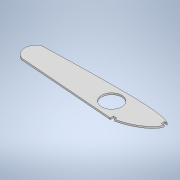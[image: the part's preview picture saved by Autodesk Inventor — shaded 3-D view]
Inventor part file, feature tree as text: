
AUTODESK INVENTOR PART (.ipt)
format: ipt  version: 2022 (Build 260153000, 153)  size: 175,104 bytes
history: native  units: mm
features: extrude x1, sketch x1
ambient origin geometry x8: Origin, YZ Plane, XZ Plane, XY Plane, X Axis, Y Axis, Z Axis, Center Point
bodies: Body1 (feature_tree)
feature tree (2):
  extrude  "Extrusion4"  Depth=160.0mm
  sketch  "Sketch1"  dims[d5=160.0mm d8=160.0mm d17=5.0mm d18=5.0mm d25=6.0mm d26=5.0mm d27=5.0mm d31=34.456mm d36=5.0mm d37=5.0mm d41=23.0mm d50=368.759386mm d60=8.0mm d62=31.0mm d63=2.5mm d64=0.0mm]
